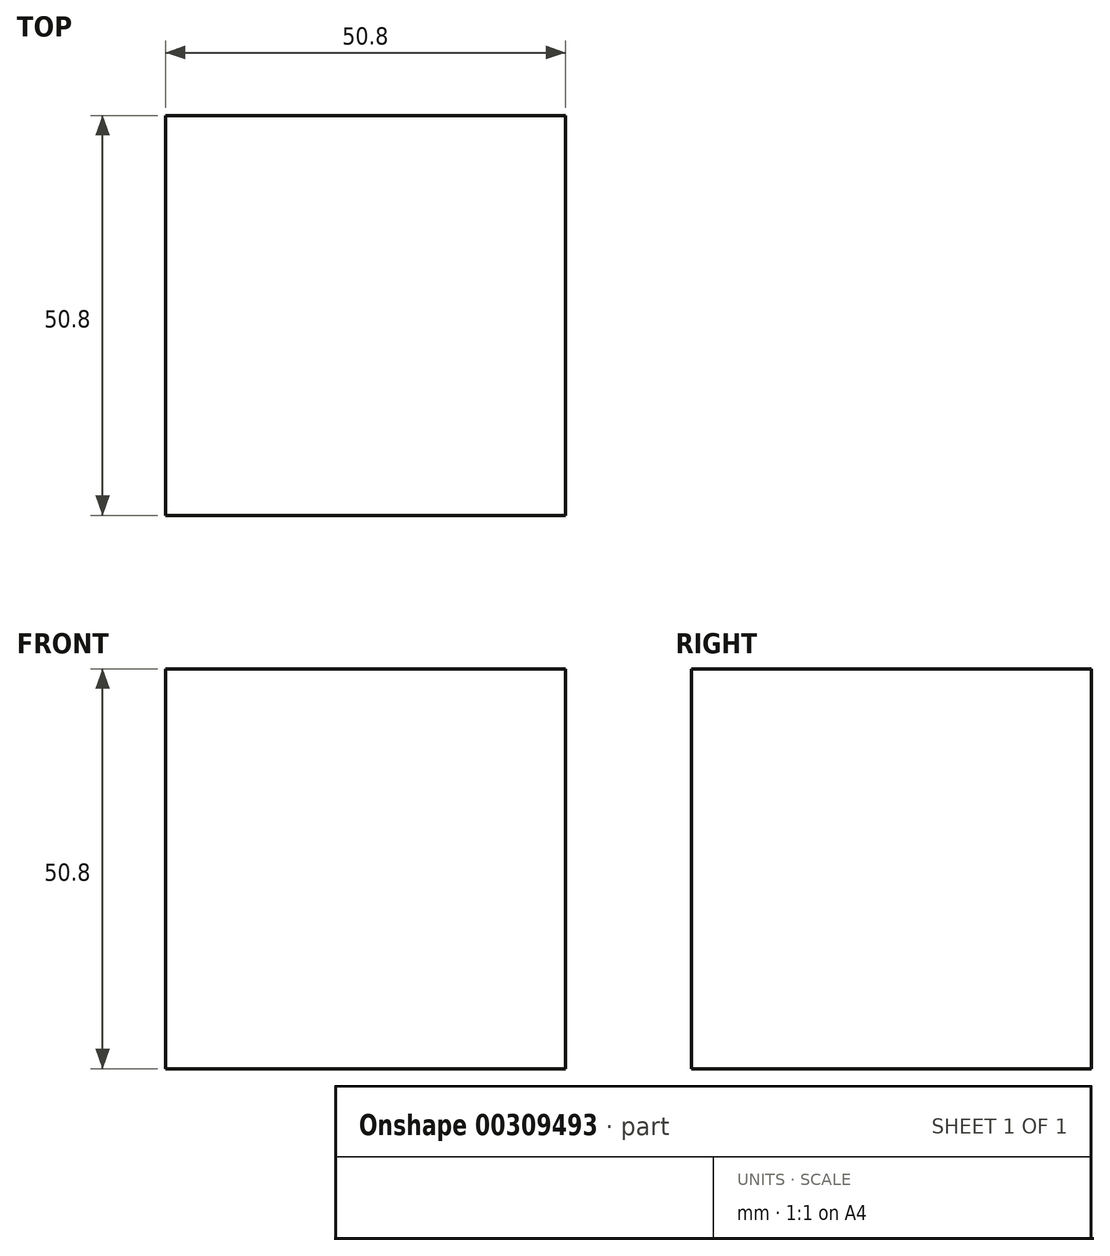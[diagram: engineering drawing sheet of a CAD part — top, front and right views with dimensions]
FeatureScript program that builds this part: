
annotation { "Feature Type Name" : "Feature", "Feature Type Description" : "" }
export const myFeature = defineFeature(function(context is Context, id is Id, definition is map)
    precondition{}
    {
        {
            var Q0;
            Q0=qCreatedBy(makeId("Front.planeOp"),FACE);
            var sketch = newSketch(context, id + "F0", { "sketchPlane" : qUnion([Q0])});
            skLineSegment(sketch, "E0.bottom", {"start": v(-25.4, 23.67) * mm, "end": v(25.4, 23.67) * mm});
            skLineSegment(sketch, "E0.top", {"start": v(-25.4, -27.13) * mm, "end": v(25.4, -27.13) * mm});
            skLineSegment(sketch, "E0.left", {"start": v(-25.4, 23.67) * mm, "end": v(-25.4, -27.13) * mm});
            skLineSegment(sketch, "E0.right", {"start": v(25.4, 23.67) * mm, "end": v(25.4, -27.13) * mm});
            skPoint(sketch, "E0.middle", {"position": v(0, -1.73) * mm});
            skSolve(sketch);
        }
        {
            var Q0;
            Q0 = qSketchRegion(id + "F0", true);
            extrude(context, id + "F1", {"entities" : qUnion([Q0]), "depth" : 50.8 * mm});
        }
    });
